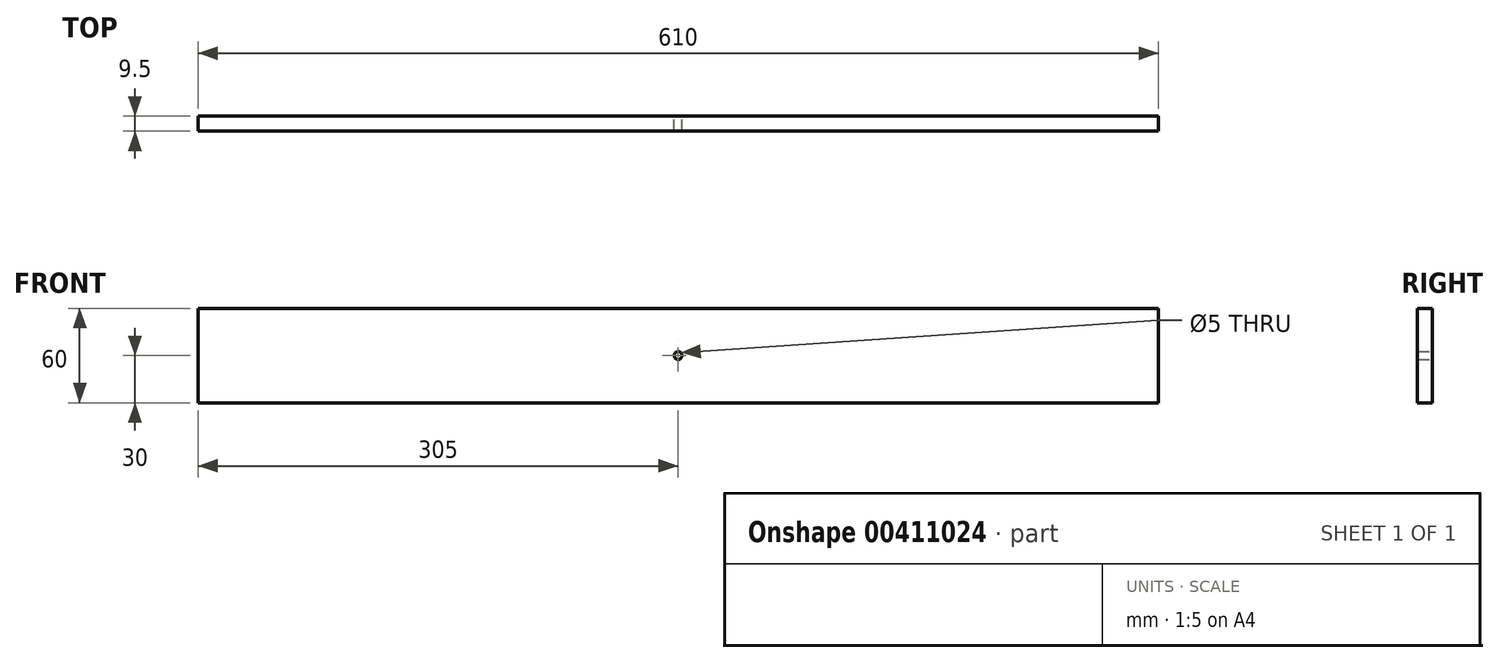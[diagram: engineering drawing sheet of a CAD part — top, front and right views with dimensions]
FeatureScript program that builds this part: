
annotation { "Feature Type Name" : "Feature", "Feature Type Description" : "" }
export const myFeature = defineFeature(function(context is Context, id is Id, definition is map)
    precondition{}
    {
        {
            var Q0;
            Q0=qCreatedBy(makeId("Right.planeOp"),FACE);
            var sketch = newSketch(context, id + "F0", { "sketchPlane" : qUnion([Q0])});
            skLineSegment(sketch, "E0.bottom", {"start": v(4.75, 30) * mm, "end": v(-4.75, 30) * mm});
            skLineSegment(sketch, "E0.top", {"start": v(4.75, -30) * mm, "end": v(-4.75, -30) * mm});
            skLineSegment(sketch, "E0.left", {"start": v(4.75, 30) * mm, "end": v(4.75, -30) * mm});
            skLineSegment(sketch, "E0.right", {"start": v(-4.75, 30) * mm, "end": v(-4.75, -30) * mm});
            skPoint(sketch, "E0.middle", {"position": v(0, 0) * mm});
            skSolve(sketch);
        }
        {
            var Q0;
            Q0 = qSketchRegion(id + "F0", true);
            extrude(context, id + "F1", {"entities" : qUnion([Q0]), "depth" : 305 * mm, "hasSecondDirection" : true, "secondDirectionOppositeDirection" : true, "secondDirectionDepth" : 305 * mm});
        }
        {
            var Q0;
            Q0=qCreatedBy(makeId("Front.planeOp"),FACE);
            var sketch = newSketch(context, id + "F2", { "sketchPlane" : qUnion([Q0])});
            skCircle(sketch, "E1", {"center": v(0, 0) * mm, "radius": 2.5 * mm});
            skSolve(sketch);
        }
        {
            var Q0;
            Q0 = qSketchRegion(id + "F2", true);
            extrude(context, id + "F3", {"entities" : qUnion([Q0]), "operationType" : NewBodyOperationType.REMOVE, "endBound" : BoundingType.UP_TO_NEXT, "depth" : 25 * mm, "hasSecondDirection" : true, "secondDirectionBound" : SecondDirectionBoundingType.UP_TO_NEXT, "secondDirectionOppositeDirection" : true, "secondDirectionDepth" : 25 * mm});
        }
    });
